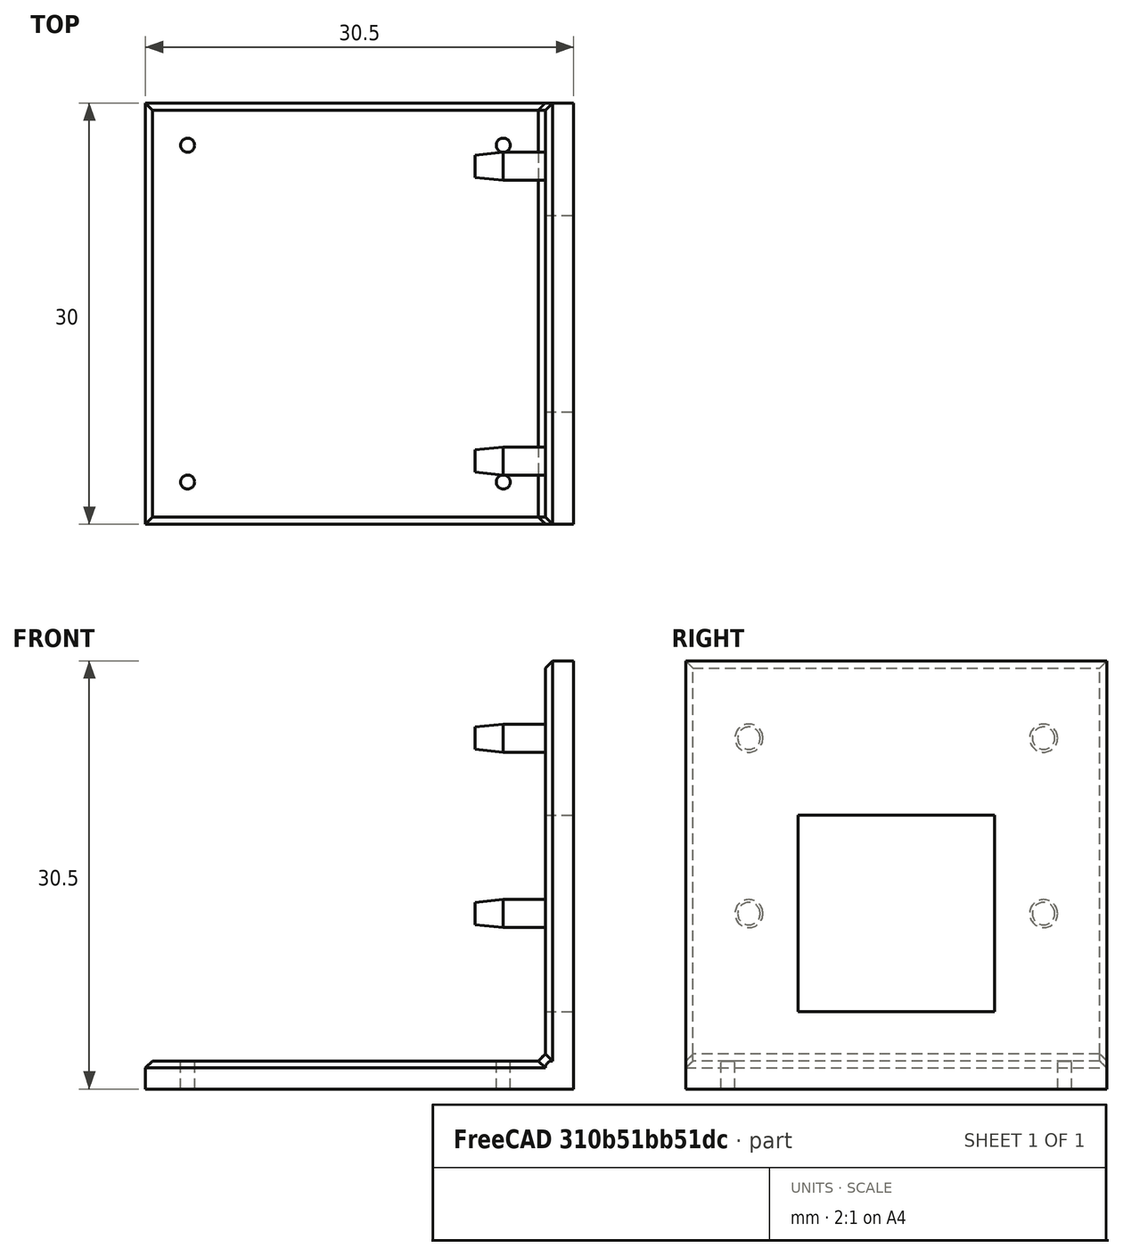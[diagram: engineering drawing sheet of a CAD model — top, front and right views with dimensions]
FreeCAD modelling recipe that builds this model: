
FCSTD DOCUMENT  (FreeCAD 0.15R4671 (Git))
Label: camera-bracket
License: All rights reserved
LicenseURL: http://en.wikipedia.org/wiki/All_rights_reserved
objects: Part::Cylinder×8, Part::Chamfer×5, Part::Box×3, Part::MultiFuse×3, Part::Cut×2
note: 21 computed .brp shape members not serialized (recipe doc carries the construction recipe); baked Part::Feature solids carry a one-line shape summary decoded from their .brp

FEATURE [Part::Box] Box001  label="Face"
  Height = 30.5
  Length = 2
  Placement = pos=(-2,0,-30.5) rot=(0,0,1;0rad)
  Width = 30
FEATURE [Part::Box] Box002  label="Window"
  Height = 14
  Length = 2
  Placement = pos=(-2,8,-25) rot=(0,0,1;0rad)
  Width = 14
FEATURE [Part::Box] Box003  label="Base"
  Height = 2
  Length = 30.5
  Placement = pos=(-30.5,0,-30.5) rot=(0,0,1;0rad)
  Width = 30
FEATURE [Part::Cylinder] Cylinder  label="Pin.1"
  Angle = 360
  Height = 7
  Placement = pos=(-7,4.5,-18) rot=(0,1,0;1.5708rad)
  Radius = 1
FEATURE [Part::Cylinder] Cylinder001  label="Pin.2"
  Angle = 360
  Height = 7
  Placement = pos=(-7,4.5,-5.5) rot=(0,1,0;1.5708rad)
  Radius = 1
FEATURE [Part::Cylinder] Cylinder002  label="Pin.3"
  Angle = 360
  Height = 7
  Placement = pos=(-7,25.5,-18) rot=(0,1,0;1.5708rad)
  Radius = 1
FEATURE [Part::Cylinder] Cylinder003  label="Pin.4"
  Angle = 360
  Height = 7
  Placement = pos=(-7,25.5,-5.5) rot=(0,1,0;1.5708rad)
  Radius = 1
FEATURE [Part::Chamfer] Chamfer  label="ChamferedPin.1"
  Base = -> Cylinder
  Edges = 1 edges: [Edge3 r1=2 r2=0.2]
FEATURE [Part::Chamfer] Chamfer001  label="ChamferedPin.2"
  Base = -> Cylinder001
  Edges = 1 edges: [Edge3 r1=2 r2=0.2]
FEATURE [Part::Chamfer] Chamfer002  label="ChamferedPin.3"
  Base = -> Cylinder002
  Edges = 1 edges: [Edge3 r1=2 r2=0.2]
FEATURE [Part::Chamfer] Chamfer003  label="ChamferedPin.4"
  Base = -> Cylinder003
  Edges = 1 edges: [Edge3 r1=2 r2=0.2]
FEATURE [Part::Cut] Cut  label="WindowedFace"
  Base = -> Box001
  Tool = -> Box002
FEATURE [Part::MultiFuse] Fusion  label="PinnedFace"
  Shapes = -> [Cut,Chamfer,Chamfer001,Chamfer002,Chamfer003]
FEATURE [Part::Cylinder] Cylinder004  label="Hole.1"
  Angle = 360
  Height = 2
  Placement = pos=(-5,3,-30.5) rot=(0,0,1;0rad)
  Radius = 0.5
FEATURE [Part::Cylinder] Cylinder005  label="Hole.2"
  Angle = 360
  Height = 2
  Placement = pos=(-27.5,3,-30.5) rot=(0,0,1;0rad)
  Radius = 0.5
FEATURE [Part::Cylinder] Cylinder006  label="Hole.3"
  Angle = 360
  Height = 2
  Placement = pos=(-5,27,-30.5) rot=(0,0,1;0rad)
  Radius = 0.5
FEATURE [Part::Cylinder] Cylinder007  label="Hole.4"
  Angle = 360
  Height = 2
  Placement = pos=(-27.5,27,-30.5) rot=(0,0,1;0rad)
  Radius = 0.5
FEATURE [Part::MultiFuse] Fusion001  label="Holes"
  Shapes = -> [Cylinder004,Cylinder005,Cylinder006,Cylinder007]
FEATURE [Part::Cut] Cut001  label="HoleBase"
  Base = -> Box003
  Tool = -> Fusion001
FEATURE [Part::MultiFuse] Fusion002  label="CameraBracket"
  Shapes = -> [Fusion,Cut001]
FEATURE [Part::Chamfer] Chamfer004  label="ChamferedCameraBracket"
  Base = -> Fusion002
  Edges = 7 edges r=0.5: [Edge1,Edge5,Edge6,Edge7,Edge29,Edge30,Edge31]
